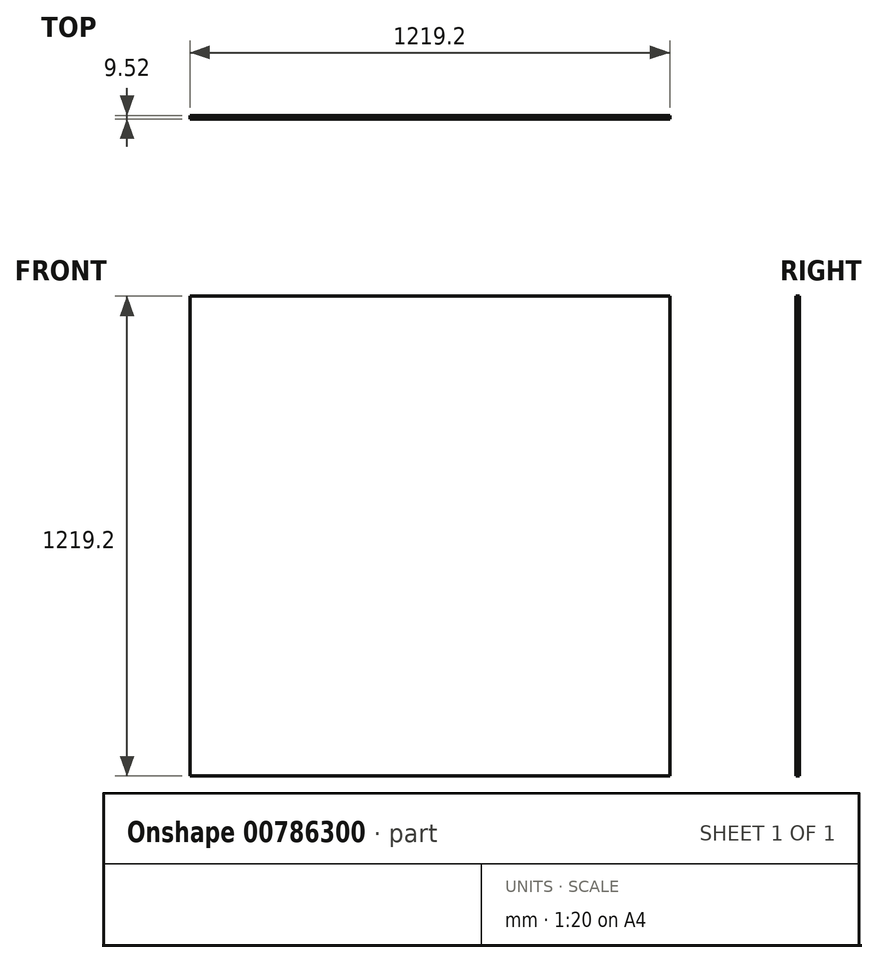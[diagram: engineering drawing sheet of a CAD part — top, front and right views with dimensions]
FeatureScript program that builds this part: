
annotation { "Feature Type Name" : "Feature", "Feature Type Description" : "" }
export const myFeature = defineFeature(function(context is Context, id is Id, definition is map)
    precondition{}
    {
        {
            var Q0;
            Q0=qCreatedBy(makeId("Front.planeOp"),FACE);
            var sketch = newSketch(context, id + "F0", { "sketchPlane" : qUnion([Q0])});
            skLineSegment(sketch, "E0.bottom", {"start": v(-609.6, 609.6) * mm, "end": v(609.6, 609.6) * mm});
            skLineSegment(sketch, "E0.top", {"start": v(-609.6, -609.6) * mm, "end": v(609.6, -609.6) * mm});
            skLineSegment(sketch, "E0.left", {"start": v(-609.6, 609.6) * mm, "end": v(-609.6, -609.6) * mm});
            skLineSegment(sketch, "E0.right", {"start": v(609.6, 609.6) * mm, "end": v(609.6, -609.6) * mm});
            skPoint(sketch, "E0.middle", {"position": v(0, 0) * mm});
            skSolve(sketch);
        }
        {
            var Q0;
            Q0=makeQuery(id+"F0.imprint","IMPRINT",FACE,{"disambiguationData":[TD([[makeQuery(id+"F0.imprint","IMPRINT",EDGE,{"derivedFrom":sQuery(id+"F0.wireOp",EDGE,"E0.bottom")}),-1.0]])]});
            extrude(context, id + "F1", {"entities" : qUnion([Q0]), "endBound" : BoundingType.SYMMETRIC, "depth" : 9.52 * mm, "offsetDistance" : 25.4 * mm});
        }
    });
